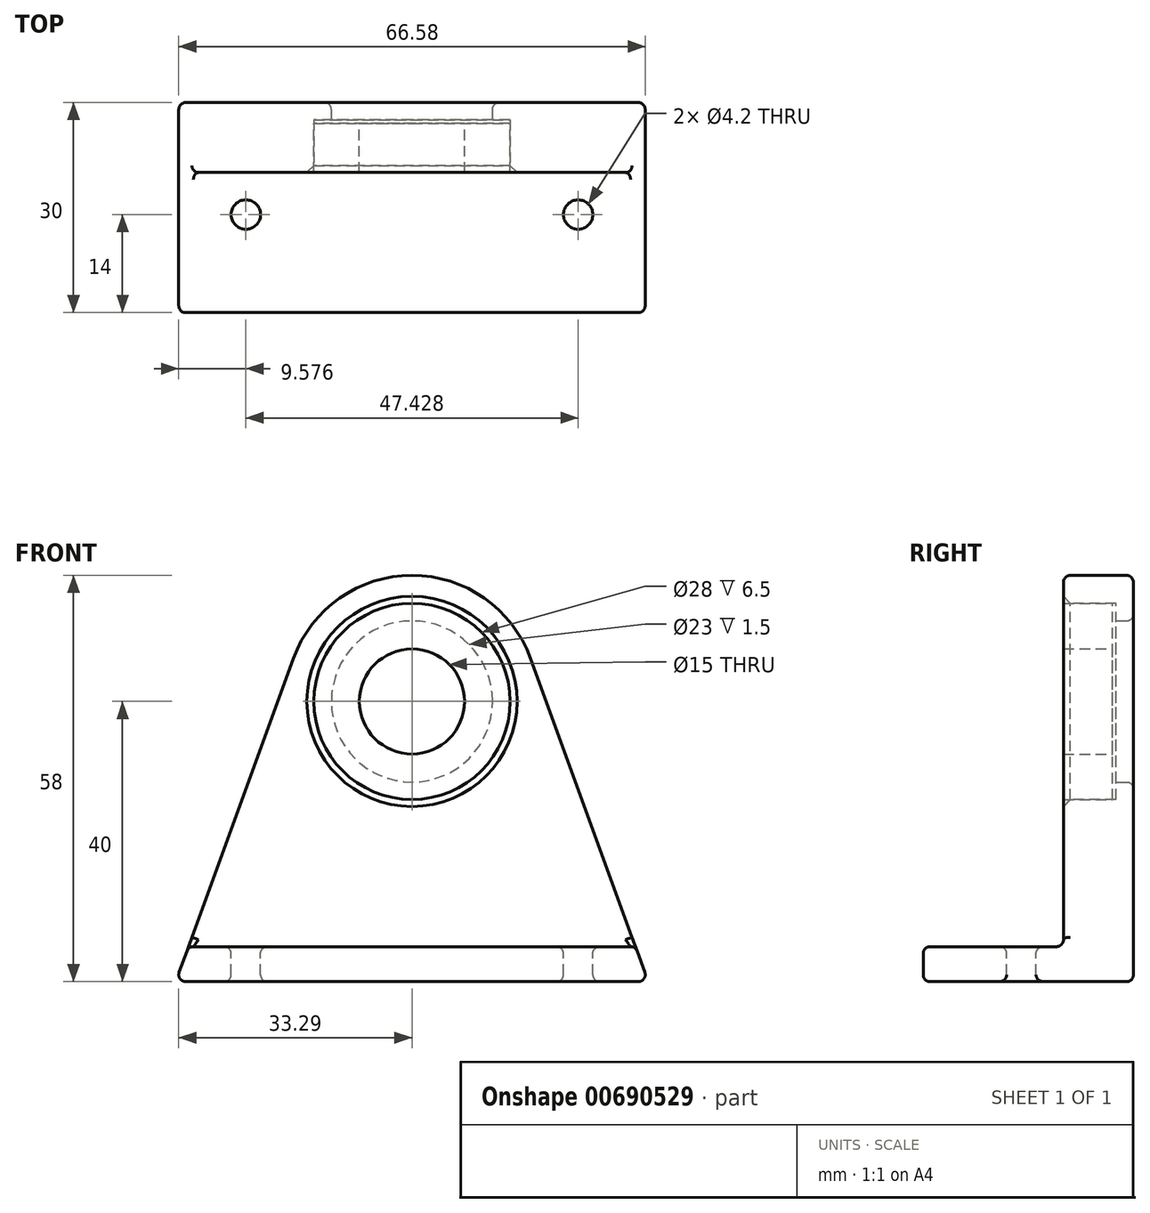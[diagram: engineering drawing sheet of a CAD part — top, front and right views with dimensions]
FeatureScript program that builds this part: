
annotation { "Feature Type Name" : "Feature", "Feature Type Description" : "" }
export const myFeature = defineFeature(function(context is Context, id is Id, definition is map)
    precondition{}
    {
        {
            var Q0;
            Q0=qCreatedBy(makeId("Front.planeOp"),FACE);
            var sketch = newSketch(context, id + "F0", { "sketchPlane" : qUnion([Q0])});
            skCircle(sketch, "E0", {"center": v(0, 0) * mm, "radius": 7.5 * mm});
            skCircle(sketch, "E1", {"center": v(0, 0) * mm, "radius": 14 * mm});
            skSolve(sketch);
        }
        {
            var Q0;
            Q0=makeQuery(id+"F0.imprint","IMPRINT",FACE,{"disambiguationData":[TD([[makeQuery(id+"F0.imprint","IMPRINT",EDGE,{"derivedFrom":sQuery(id+"F0.wireOp",EDGE,"E0")}),-1.0]])]});
            extrude(context, id + "F1", {"entities" : qUnion([Q0]), "depth" : 7 * mm, "offsetDistance" : 25 * mm});
        }
        {
            var Q0;
            Q0=makeQuery(id+"F1.opExtrude","CAP_FACE",FACE,{"disambiguationData":[OSD([sQuery(id+"F0.wireOp",EDGE,"E0"),sQuery(id+"F0.wireOp",EDGE,"E1")])],"isStart":false});
            var sketch = newSketch(context, id + "F2", { "sketchPlane" : qUnion([Q0])});
            skCircle(sketch, "E2", {"center": v(0, 0) * mm, "radius": 18 * mm});
            skLineSegment(sketch, "E3", {"start": v(-33.71, -40) * mm, "end": v(33.71, -40) * mm});
            skLineSegment(sketch, "E4", {"start": v(-33.71, -40) * mm, "end": v(-16.91, 6.16) * mm});
            skLineSegment(sketch, "E5", {"start": v(16.91, 6.16) * mm, "end": v(33.71, -40) * mm});
            skSolve(sketch);
        }
        {
            var Q0;
            Q0=makeQuery(id+"F2.imprint","IMPRINT",FACE,{"disambiguationData":[TD([[makeQuery(id+"F2.imprint","IMPRINT",EDGE,{"derivedFrom":sQuery(id+"F2.wireOp",EDGE,"E3")}),1.0]])]});
            var Q1;
            Q1=makeQuery(id+"F2.imprint","IMPRINT",FACE,{"disambiguationData":[TD([[makeQuery(id+"F2.imprint","IMPRINT",EDGE,{"derivedFrom":makeQuery(id+"F1.opExtrude","CAP_EDGE",EDGE,{"disambiguationData":[OSD([sQuery(id+"F0.wireOp",EDGE,"E1")])],"isStart":false})}),-1.0]])]});
            extrude(context, id + "F3", {"entities" : qUnion([Q0, Q1]), "oppositeDirection" : true, "depth" : (7 + 3) * mm, "offsetDistance" : 25 * mm});
        }
        {
            var Q0;
            Q0=makeQuery(id+"F3.opExtrude","CAP_FACE",FACE,{"disambiguationData":[OSD([sQuery(id+"F0.wireOp",EDGE,"E1"),sQuery(id+"F2.wireOp",EDGE,"E2"),sQuery(id+"F2.wireOp",EDGE,"E3"),sQuery(id+"F2.wireOp",EDGE,"E4"),sQuery(id+"F2.wireOp",EDGE,"E5")])],"isStart":false});
            var sketch = newSketch(context, id + "F4", { "sketchPlane" : qUnion([Q0])});
            skCircle(sketch, "E6", {"center": v(0, 0) * mm, "radius": 14 * mm});
            skCircle(sketch, "E7", {"center": v(0, 0) * mm, "radius": 11.5 * mm});
            skSolve(sketch);
        }
        {
            var Q0;
            Q0=makeQuery(id+"F4.imprint","IMPRINT",FACE,{"disambiguationData":[TD([[makeQuery(id+"F4.imprint","IMPRINT",EDGE,{"derivedFrom":sQuery(id+"F4.wireOp",EDGE,"E6")}),-1.0]])]});
            var Q1;
            Q1=makeQuery(id+"F1.opExtrude","CAP_FACE",FACE,{"disambiguationData":[OSD([sQuery(id+"F0.wireOp",EDGE,"E0"),sQuery(id+"F0.wireOp",EDGE,"E1")])],"isStart":true});
            extrude(context, id + "F5", {"entities" : qUnion([Q0]), "operationType" : NewBodyOperationType.ADD, "endBound" : BoundingType.UP_TO_SURFACE, "oppositeDirection" : true, "depth" : 25 * mm, "endBoundEntityFace" : qUnion([Q1]), "hasOffset" : true, "offsetDistance" : 0.5 * mm});
        }
        {
            var Q0;
            Q0=makeQuery(id+"F3.opExtrude","CAP_FACE",FACE,{"disambiguationData":[OSD([sQuery(id+"F0.wireOp",EDGE,"E1"),sQuery(id+"F2.wireOp",EDGE,"E2"),sQuery(id+"F2.wireOp",EDGE,"E3"),sQuery(id+"F2.wireOp",EDGE,"E4"),sQuery(id+"F2.wireOp",EDGE,"E5")])],"isStart":true});
            var sketch = newSketch(context, id + "F6", { "sketchPlane" : qUnion([Q0])});
            skLineSegment(sketch, "E8", {"start": v(-33.71, -40) * mm, "end": v(33.71, -40) * mm});
            skLineSegment(sketch, "E9", {"start": v(33.71, -40) * mm, "end": v(31.9, -35) * mm});
            skLineSegment(sketch, "E10", {"start": v(31.9, -35) * mm, "end": v(-31.9, -35) * mm});
            skLineSegment(sketch, "E11", {"start": v(-31.9, -35) * mm, "end": v(-33.71, -40) * mm});
            skSolve(sketch);
        }
        {
            var Q0;
            Q0=qSketchRegion(id+"F6",true);
            extrude(context, id + "F7", {"entities" : qUnion([Q0]), "operationType" : NewBodyOperationType.ADD, "depth" : 20 * mm, "offsetDistance" : 25 * mm});
        }
        {
            var Q0;
            Q0=makeQuery(id+"F7.opExtrude","SWEPT_FACE",FACE,{"disambiguationData":[OSD([sQuery(id+"F6.wireOp",EDGE,"E10")])]});
            var sketch = newSketch(context, id + "F8", { "sketchPlane" : qUnion([Q0])});
            skCircle(sketch, "E12", {"center": v(-23.71, -13) * mm, "radius": 2.1 * mm});
            skCircle(sketch, "E13", {"center": v(23.71, -13) * mm, "radius": 2.1 * mm});
            skSolve(sketch);
        }
        {
            var Q0;
            Q0=makeQuery(id+"F8.imprint","IMPRINT",FACE,{"disambiguationData":[TD([[makeQuery(id+"F8.imprint","IMPRINT",EDGE,{"derivedFrom":sQuery(id+"F8.wireOp",EDGE,"E12")}),1.0]])]});
            var Q1;
            Q1=makeQuery(id+"F8.imprint","IMPRINT",FACE,{"disambiguationData":[TD([[makeQuery(id+"F8.imprint","IMPRINT",EDGE,{"derivedFrom":sQuery(id+"F8.wireOp",EDGE,"E13")}),1.0]])]});
            extrude(context, id + "F9", {"entities" : qUnion([Q0, Q1]), "operationType" : NewBodyOperationType.REMOVE, "oppositeDirection" : true, "depth" : 25 * mm, "offsetDistance" : 25 * mm});
        }
        {
            var Q0;
            Q0=makeQuery(id+"F7.boolean.opBoolean","MERGE",FACE,{"derivedFrom":[makeQuery(id+"F3.opExtrude","SWEPT_FACE",FACE,{"disambiguationData":[OSD([sQuery(id+"F2.wireOp",EDGE,"E4")])]}),makeQuery(id+"F7.opExtrude","SWEPT_FACE",FACE,{"disambiguationData":[OSD([sQuery(id+"F6.wireOp",EDGE,"E11")])]})]});
            var Q1;
            Q1=makeQuery(id+"F3.opExtrude","SWEPT_FACE",FACE,{"disambiguationData":[OSD([sQuery(id+"F2.wireOp",EDGE,"E2")])]});
            var Q2;
            Q2=makeQuery(id+"F7.boolean.opBoolean","MERGE",FACE,{"derivedFrom":[makeQuery(id+"F3.opExtrude","SWEPT_FACE",FACE,{"disambiguationData":[OSD([sQuery(id+"F2.wireOp",EDGE,"E5")])]}),makeQuery(id+"F7.opExtrude","SWEPT_FACE",FACE,{"disambiguationData":[OSD([sQuery(id+"F6.wireOp",EDGE,"E9")])]})]});
            var Q3;
            Q3=makeQuery(id+"F7.opExtrude","SWEPT_FACE",FACE,{"disambiguationData":[OSD([sQuery(id+"F6.wireOp",EDGE,"E10")])]});
            var Q4;
            Q4=makeQuery(id+"F7.opExtrude","CAP_FACE",FACE,{"disambiguationData":[OSD([sQuery(id+"F6.wireOp",EDGE,"E8"),sQuery(id+"F6.wireOp",EDGE,"E9"),sQuery(id+"F6.wireOp",EDGE,"E10"),sQuery(id+"F6.wireOp",EDGE,"E11")])],"isStart":false});
            var Q5;
            Q5=makeQuery(id+"F7.boolean.opBoolean","MERGE",FACE,{"derivedFrom":[makeQuery(id+"F3.opExtrude","SWEPT_FACE",FACE,{"disambiguationData":[OSD([sQuery(id+"F2.wireOp",EDGE,"E3")])]}),makeQuery(id+"F7.opExtrude","SWEPT_FACE",FACE,{"disambiguationData":[OSD([sQuery(id+"F6.wireOp",EDGE,"E8")])]})]});
            var Q6;
            Q6=makeQuery(id+"F5.boolean.opBoolean","MERGE",FACE,{"derivedFrom":[makeQuery(id+"F3.opExtrude","CAP_FACE",FACE,{"disambiguationData":[OSD([sQuery(id+"F0.wireOp",EDGE,"E1"),sQuery(id+"F2.wireOp",EDGE,"E2"),sQuery(id+"F2.wireOp",EDGE,"E3"),sQuery(id+"F2.wireOp",EDGE,"E4"),sQuery(id+"F2.wireOp",EDGE,"E5")])],"isStart":false}),makeQuery(id+"F5.opExtrude","CAP_FACE",FACE,{"disambiguationData":[OSD([sQuery(id+"F4.wireOp",EDGE,"E6"),sQuery(id+"F4.wireOp",EDGE,"E7")])],"isStart":true})]});
            fillet(context, id + "F10", {"entities" : qUnion([Q0, Q1, Q2, Q3, Q4, Q5, Q6]), "radius" : 1 * mm, "tangentPropagation" : true, "allowEdgeOverflow" : false});
        }
        {
            var Q0;
            Q0=makeQuery(id+"F3.opExtrude","CAP_EDGE",EDGE,{"disambiguationData":[OSD([sQuery(id+"F0.wireOp",EDGE,"E1")])],"isStart":true});
            chamfer(context, id + "F11", {"entities" : qUnion([Q0]), "width" : 1 * mm, "tangentPropagation" : true});
        }
    });
